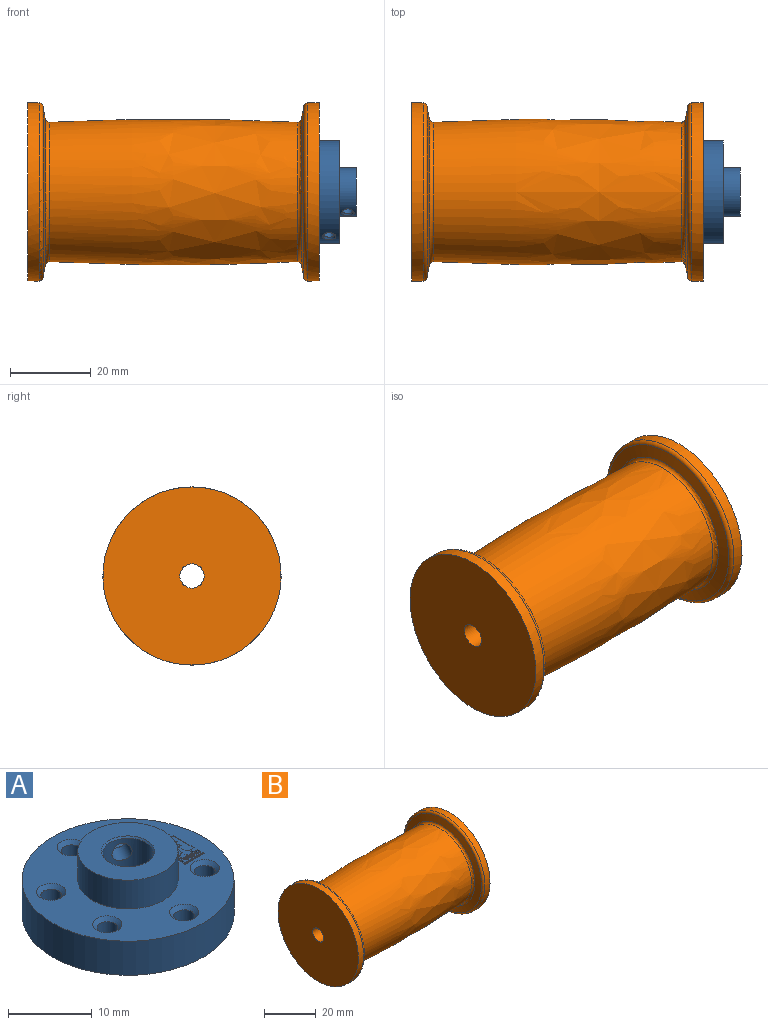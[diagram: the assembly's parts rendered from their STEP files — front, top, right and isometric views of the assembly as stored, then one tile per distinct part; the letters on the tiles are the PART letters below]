
ASSEMBLY  parts=2 mates=1
PART A: 277 faces, bbox 25.4x25.4x9.2 mm
  f0: bspline ~3.27x2.94mm, area 5.6mm2, adj f17,f26
  f1: bspline ~3.07x2.86mm, area 4.8mm2, adj f16,f19
  f2: cone r=3mm half-angle=45deg, axis (0,0,1), area 5.5mm2, adj f18,f29
  f3: cone r=3.2mm half-angle=45deg, axis (0,0,-1), area 5.5mm2, adj f18,f28
  f4: cone r=1.25mm half-angle=45deg, axis (0,0,1), area 6.7mm2, adj f25,f27
  f5: cone r=1.25mm half-angle=45deg, axis (0,0,1), area 6.7mm2, adj f24,f27
  f6: cone r=1.25mm half-angle=45deg, axis (0,0,1), area 6.7mm2, adj f23,f27
  f7: cone r=1.25mm half-angle=45deg, axis (0,0,1), area 6.7mm2, adj f22,f27
  f8: cone r=1.25mm half-angle=45deg, axis (0,0,1), area 6.7mm2, adj f21,f27
  f9: cone r=1.25mm half-angle=45deg, axis (0,0,1), area 6.7mm2, adj f20,f27
  f10: cone r=1.75mm half-angle=45deg, axis (0,0,-1), area 6.7mm2, adj f20,f28
  f11: cone r=1.75mm half-angle=45deg, axis (0,0,-1), area 6.7mm2, adj f25,f28
  f12: cone r=1.75mm half-angle=45deg, axis (0,0,-1), area 6.7mm2, adj f24,f28
  f13: cone r=1.75mm half-angle=45deg, axis (0,0,-1), area 6.7mm2, adj f23,f28
  f14: cone r=1.75mm half-angle=45deg, axis (0,0,-1), area 6.7mm2, adj f22,f28
  f15: cone r=1.75mm half-angle=45deg, axis (0,0,-1), area 6.7mm2, adj f21,f28
  f16: cylinder r=1.25mm len=3.72mm, axis (0.5,0.87,0), area 20.5mm2, adj f1,f18
  f17: cylinder r=1.25mm len=9.5mm, axis (0.5,0.87,0), area 73.3mm2, adj f0,f18
  f18: cylinder r=3mm len=8.8mm, axis (0,0,1), area 155.8mm2, adj f2,f3,f16,f17
  f19: cylinder r=6mm len=12mm, axis (0,0,-1), area 150.3mm2, adj f1,f27,f29
  f20: cylinder r=1.25mm len=4mm, axis (0,0,1), area 31.4mm2, adj f9,f10
  f21: cylinder r=1.25mm len=4mm, axis (0,0,1), area 31.4mm2, adj f8,f15
  f22: cylinder r=1.25mm len=4mm, axis (0,0,1), area 31.4mm2, adj f7,f14
  f23: cylinder r=1.25mm len=4mm, axis (0,0,1), area 31.4mm2, adj f6,f13
  f24: cylinder r=1.25mm len=4mm, axis (0,0,1), area 31.4mm2, adj f5,f12
  f25: cylinder r=1.25mm len=4mm, axis (0,0,1), area 31.4mm2, adj f4,f11
  f26: cylinder r=12.7mm len=25.4mm, axis (0,0,-1), area 390.2mm2, adj f0,f27,f28
  f27: plane 25.4x25.4mm, normal (0,0,1), area 325.6mm2, adj f4,f5,f6,f7,f8,f9,f19,f26
  f28: plane 25.4x25.4mm, normal (0,0,-1), area 416.8mm2, adj f3,f10,f11,f12,f13,f14,f15,f26
  f29: plane 12x12mm, normal (0,0,1), area 80.9mm2, adj f2,f19
  f30: plane 0.05x0.04mm, normal (0,-1,0), area 0mm2, adj f27,f31,f42,f43
  f31: plane 0.22x0.06mm, normal (-0.97,0.25,0), area 0mm2, adj f27,f30,f32,f43
  f32: plane 0.05x0.03mm, normal (0,1,0), area 0mm2, adj f27,f31,f33,f43
  f33: plane 0.17x0.06mm, normal (0.95,0.31,0), area 0mm2, adj f27,f32,f34,f43
  f34: plane 0.17x0.06mm, normal (-0.95,0.31,0), area 0mm2, adj f27,f33,f35,f43
  f35: plane 0.05x0.03mm, normal (0,1,0), area 0mm2, adj f27,f34,f36,f43
  f36: plane 0.22x0.06mm, normal (0.97,0.25,0), area 0mm2, adj f27,f35,f37,f43
  f37: plane 0.05x0.04mm, normal (0,-1,0), area 0mm2, adj f27,f36,f38,f43
  f38: plane 0.17x0.05mm, normal (-0.97,-0.23,0), area 0mm2, adj f27,f37,f39,f43
  f39: plane 0.17x0.06mm, normal (0.95,-0.31,0), area 0mm2, adj f27,f38,f40,f43
  f40: plane 0.05x0.03mm, normal (0,-1,0), area 0mm2, adj f27,f39,f41,f43
  f41: plane 0.17x0.06mm, normal (-0.95,-0.31,0), area 0mm2, adj f27,f40,f42,f43
  f42: plane 0.17x0.05mm, normal (0.98,-0.21,0), area 0mm2, adj f27,f30,f41,f43
  f43: plane 0.3x0.22mm, normal (0,0,1), area 0mm2, adj f30,f31,f32,f33,f34,f35,f36,f37
  f44: plane 0.05x0.04mm, normal (0,-1,0), area 0mm2, adj f27,f45,f56,f57
  f45: plane 0.22x0.06mm, normal (-0.97,0.25,0), area 0mm2, adj f27,f44,f46,f57
  f46: plane 0.05x0.03mm, normal (0,1,0), area 0mm2, adj f27,f45,f47,f57
  f47: plane 0.17x0.06mm, normal (0.95,0.31,0), area 0mm2, adj f27,f46,f48,f57
  f48: plane 0.17x0.06mm, normal (-0.95,0.31,0), area 0mm2, adj f27,f47,f49,f57
  f49: plane 0.05x0.03mm, normal (0,1,0), area 0mm2, adj f27,f48,f50,f57
  f50: plane 0.22x0.06mm, normal (0.97,0.25,0), area 0mm2, adj f27,f49,f51,f57
  f51: plane 0.05x0.04mm, normal (0,-1,0), area 0mm2, adj f27,f50,f52,f57
  f52: plane 0.17x0.05mm, normal (-0.97,-0.23,0), area 0mm2, adj f27,f51,f53,f57
  f53: plane 0.17x0.06mm, normal (0.95,-0.31,0), area 0mm2, adj f27,f52,f54,f57
  f54: plane 0.05x0.03mm, normal (0,-1,0), area 0mm2, adj f27,f53,f55,f57
  f55: plane 0.17x0.06mm, normal (-0.95,-0.31,0), area 0mm2, adj f27,f54,f56,f57
  f56: plane 0.17x0.05mm, normal (0.98,-0.21,0), area 0mm2, adj f27,f44,f55,f57
  f57: plane 0.3x0.22mm, normal (0,0,1), area 0mm2, adj f44,f45,f46,f47,f48,f49,f50,f51
  f58: plane 0.05x0.04mm, normal (0,-1,0), area 0mm2, adj f27,f59,f70,f71
  f59: plane 0.22x0.06mm, normal (-0.97,0.25,0), area 0mm2, adj f27,f58,f60,f71
  f60: plane 0.05x0.03mm, normal (0,1,0), area 0mm2, adj f27,f59,f61,f71
  f61: plane 0.17x0.06mm, normal (0.95,0.31,0), area 0mm2, adj f27,f60,f62,f71
  f62: plane 0.17x0.06mm, normal (-0.95,0.31,0), area 0mm2, adj f27,f61,f63,f71
  f63: plane 0.05x0.03mm, normal (0,1,0), area 0mm2, adj f27,f62,f64,f71
  f64: plane 0.22x0.06mm, normal (0.97,0.25,0), area 0mm2, adj f27,f63,f65,f71
  f65: plane 0.05x0.04mm, normal (0,-1,0), area 0mm2, adj f27,f64,f66,f71
  f66: plane 0.17x0.05mm, normal (-0.97,-0.23,0), area 0mm2, adj f27,f65,f67,f71
  f67: plane 0.17x0.06mm, normal (0.95,-0.31,0), area 0mm2, adj f27,f66,f68,f71
  f68: plane 0.05x0.03mm, normal (0,-1,0), area 0mm2, adj f27,f67,f69,f71
  f69: plane 0.17x0.06mm, normal (-0.95,-0.31,0), area 0mm2, adj f27,f68,f70,f71
  f70: plane 0.17x0.05mm, normal (0.98,-0.21,0), area 0mm2, adj f27,f58,f69,f71
  f71: plane 0.3x0.22mm, normal (0,0,1), area 0mm2, adj f58,f59,f60,f61,f62,f63,f64,f65
  f72: plane 0.06x0.05mm, normal (-1,0,0), area 0mm2, adj f27,f73,f75,f76
  f73: plane 0.05x0.05mm, normal (0,1,0), area 0mm2, adj f27,f72,f74,f76
  f74: plane 0.06x0.05mm, normal (1,0,0), area 0mm2, adj f27,f73,f75,f76
  f75: plane 0.05x0.05mm, normal (0,-1,0), area 0mm2, adj f27,f72,f74,f76
  f76: plane 0.06x0.05mm, normal (0,0,1), area 0mm2, adj f72,f73,f74,f75
  f77: extruded ~0.11x0.08mm, area 0mm2, adj f27,f78,f86,f87
  f78: extruded ~0.09x0.05mm, area 0mm2, adj f27,f77,f79,f87
  f79: cylinder r=0.09mm len=0.07mm, axis (0,0,-1), area 0mm2, adj f27,f78,f80,f87
  f80: cylinder r=0.11mm len=0.06mm, axis (0,0,-1), area 0mm2, adj f27,f79,f81,f87
  f81: plane 0.09x0.05mm, normal (-1,0,0), area 0mm2, adj f27,f80,f82,f87
  f82: plane 0.05x0.04mm, normal (0,1,0), area 0mm2, adj f27,f81,f83,f87
  f83: plane 0.3x0.05mm, normal (1,0,0), area 0mm2, adj f27,f82,f84,f87
  f84: plane 0.05x0.04mm, normal (0,-1,0), area 0mm2, adj f27,f83,f85,f87
  f85: plane 0.05x0.02mm, normal (-1,0,0), area 0mm2, adj f27,f84,f86,f87
  f86: extruded ~0.07x0.05mm, area 0mm2, adj f27,f77,f85,f87
  f87: plane 0.31x0.19mm, normal (0,0,1), area 0mm2, adj f77,f78,f79,f80,f81,f82,f83,f84
  f88: extruded ~0.08x0.06mm, area 0mm2, adj f87,f89,f92,f93
  f89: cylinder r=0.14mm len=0.05mm, axis (0,0,1), area 0mm2, adj f87,f88,f90,f93
  f90: plane 0.13x0.05mm, normal (-1,0,0), area 0mm2, adj f87,f89,f91,f93
  f91: extruded ~0.06x0.05mm, area 0mm2, adj f87,f90,f92,f93
  f92: extruded ~0.08x0.05mm, area 0mm2, adj f87,f88,f91,f93
  f93: plane 0.17x0.12mm, normal (0,0,1), area 0mm2, adj f88,f89,f90,f91,f92
  f94: extruded ~0.12x0.1mm, area 0mm2, adj f27,f95,f97,f98
  f95: extruded ~0.12x0.1mm, area 0mm2, adj f27,f94,f96,f98
  f96: extruded ~0.12x0.1mm, area 0mm2, adj f27,f95,f97,f98
  f97: extruded ~0.12x0.1mm, area 0mm2, adj f27,f94,f96,f98
  f98: plane 0.24x0.2mm, normal (0,0,1), area 0mm2, adj f94,f95,f96,f97,f99,f100,f101,f102
  f99: extruded ~0.08x0.06mm, area 0mm2, adj f98,f100,f102,f103
  f100: extruded ~0.08x0.06mm, area 0mm2, adj f98,f99,f101,f103
  f101: extruded ~0.08x0.06mm, area 0mm2, adj f98,f100,f102,f103
  f102: extruded ~0.08x0.06mm, area 0mm2, adj f98,f99,f101,f103
  f103: plane 0.17x0.13mm, normal (0,0,1), area 0mm2, adj f99,f100,f101,f102
  f104: plane 0.31x0.05mm, normal (-1,0,0), area 0mm2, adj f27,f105,f107,f108
  f105: plane 0.05x0.04mm, normal (0,1,0), area 0mm2, adj f27,f104,f106,f108
  f106: plane 0.31x0.05mm, normal (1,0,0), area 0mm2, adj f27,f105,f107,f108
  f107: plane 0.05x0.04mm, normal (0,-1,0), area 0mm2, adj f27,f104,f106,f108
  f108: plane 0.31x0.04mm, normal (0,0,1), area 0mm2, adj f104,f105,f106,f107
  f109: extruded ~0.12x0.1mm, area 0mm2, adj f27,f110,f112,f113
  f110: extruded ~0.12x0.1mm, area 0mm2, adj f27,f109,f111,f113
  f111: extruded ~0.12x0.1mm, area 0mm2, adj f27,f110,f112,f113
  f112: extruded ~0.12x0.1mm, area 0mm2, adj f27,f109,f111,f113
  f113: plane 0.24x0.2mm, normal (0,0,1), area 0mm2, adj f109,f110,f111,f112,f114,f115,f116,f117
  f114: extruded ~0.08x0.06mm, area 0mm2, adj f113,f115,f117,f118
  f115: extruded ~0.08x0.06mm, area 0mm2, adj f113,f114,f116,f118
  f116: extruded ~0.08x0.06mm, area 0mm2, adj f113,f115,f117,f118
  f117: extruded ~0.08x0.06mm, area 0mm2, adj f113,f114,f116,f118
  f118: plane 0.17x0.13mm, normal (0,0,1), area 0mm2, adj f114,f115,f116,f117
  f119: plane 0.31x0.05mm, normal (-1,0,0), area 0mm2, adj f27,f120,f122,f123
  f120: plane 0.05x0.04mm, normal (0,1,0), area 0mm2, adj f27,f119,f121,f123
  f121: plane 0.31x0.05mm, normal (1,0,0), area 0mm2, adj f27,f120,f122,f123
  f122: plane 0.05x0.04mm, normal (0,-1,0), area 0mm2, adj f27,f119,f121,f123
  f123: plane 0.31x0.04mm, normal (0,0,1), area 0mm2, adj f119,f120,f121,f122
  f124: plane 0.22x0.05mm, normal (-1,0,0), area 0mm2, adj f27,f125,f136,f137
  f125: plane 0.05x0.04mm, normal (0,1,0), area 0mm2, adj f27,f124,f126,f137
  f126: plane 0.05x0.02mm, normal (1,0,0), area 0mm2, adj f27,f125,f127,f137
  f127: extruded ~0.07x0.05mm, area 0mm2, adj f27,f126,f128,f137
  f128: extruded ~0.08x0.07mm, area 0mm2, adj f27,f127,f129,f137
  f129: plane 0.14x0.05mm, normal (1,0,0), area 0mm2, adj f27,f128,f130,f137
  f130: plane 0.05x0.04mm, normal (0,-1,0), area 0mm2, adj f27,f129,f131,f137
  f131: plane 0.13x0.05mm, normal (-1,0,0), area 0mm2, adj f27,f130,f132,f137
  f132: extruded ~0.05x0.05mm, area 0mm2, adj f27,f131,f133,f137
  f133: extruded ~0.05x0.04mm, area 0mm2, adj f27,f132,f134,f137
  f134: extruded ~0.06x0.05mm, area 0mm2, adj f27,f133,f135,f137
  f135: plane 0.17x0.05mm, normal (1,0,0), area 0mm2, adj f27,f134,f136,f137
  f136: plane 0.05x0.04mm, normal (0,-1,0), area 0mm2, adj f27,f124,f135,f137
  f137: plane 0.23x0.18mm, normal (0,0,1), area 0mm2, adj f124,f125,f126,f127,f128,f129,f130,f131
  f138: plane 0.06x0.05mm, normal (-1,0,0), area 0mm2, adj f27,f139,f141,f142
  f139: plane 0.05x0.05mm, normal (0,1,0), area 0mm2, adj f27,f138,f140,f142
  f140: plane 0.06x0.05mm, normal (1,0,0), area 0mm2, adj f27,f139,f141,f142
  f141: plane 0.05x0.05mm, normal (0,-1,0), area 0mm2, adj f27,f138,f140,f142
  f142: plane 0.06x0.05mm, normal (0,0,1), area 0mm2, adj f138,f139,f140,f141
  f143: plane 0.05x0.04mm, normal (-1,0,0), area 0mm2, adj f27,f144,f156,f157
  f144: extruded ~0.07x0.05mm, area 0mm2, adj f27,f143,f145,f157
  f145: extruded ~0.08x0.05mm, area 0mm2, adj f27,f144,f146,f157
  f146: extruded ~0.09x0.05mm, area 0mm2, adj f27,f145,f147,f157
  f147: extruded ~0.12x0.11mm, area 0mm2, adj f27,f146,f148,f157
  f148: extruded ~0.07x0.05mm, area 0mm2, adj f27,f147,f149,f157
  f149: plane 0.05x0.04mm, normal (-1,0,0), area 0mm2, adj f27,f148,f150,f157
  f150: plane 0.05x0mm, normal (0,1,0), area 0mm2, adj f27,f149,f151,f157
  f151: extruded ~0.07x0.05mm, area 0mm2, adj f27,f150,f152,f157
  f152: extruded ~0.08x0.07mm, area 0mm2, adj f27,f151,f153,f157
  f153: extruded ~0.08x0.07mm, area 0mm2, adj f27,f152,f154,f157
  f154: cylinder r=0.09mm len=0.05mm, axis (0,0,1), area 0mm2, adj f27,f153,f155,f157
  f155: cylinder r=0.16mm len=0.05mm, axis (0,0,1), area 0mm2, adj f27,f154,f156,f157
  f156: plane 0.05x0mm, normal (0,-1,0), area 0mm2, adj f27,f143,f155,f157
  f157: plane 0.23x0.18mm, normal (0,0,1), area 0mm2, adj f143,f144,f145,f146,f147,f148,f149,f150
  f158: extruded ~0.12x0.1mm, area 0mm2, adj f27,f159,f161,f162
  f159: extruded ~0.12x0.1mm, area 0mm2, adj f27,f158,f160,f162
  f160: extruded ~0.12x0.1mm, area 0mm2, adj f27,f159,f161,f162
  f161: extruded ~0.12x0.1mm, area 0mm2, adj f27,f158,f160,f162
  f162: plane 0.24x0.2mm, normal (0,0,1), area 0mm2, adj f158,f159,f160,f161,f163,f164,f165,f166
  f163: extruded ~0.08x0.06mm, area 0mm2, adj f162,f164,f166,f167
  f164: extruded ~0.08x0.06mm, area 0mm2, adj f162,f163,f165,f167
  f165: extruded ~0.08x0.06mm, area 0mm2, adj f162,f164,f166,f167
  f166: extruded ~0.08x0.06mm, area 0mm2, adj f162,f163,f165,f167
  f167: plane 0.17x0.13mm, normal (0,0,1), area 0mm2, adj f163,f164,f165,f166
  f168: plane 0.14x0.05mm, normal (-1,0,0), area 0mm2, adj f27,f169,f189,f190
  f169: plane 0.05x0.04mm, normal (0,1,0), area 0mm2, adj f27,f168,f170,f190
  f170: plane 0.13x0.05mm, normal (1,0,0), area 0mm2, adj f27,f169,f171,f190
  f171: extruded ~0.05x0.05mm, area 0mm2, adj f27,f170,f172,f190
  f172: extruded ~0.05x0.04mm, area 0mm2, adj f27,f171,f173,f190
  f173: extruded ~0.06x0.05mm, area 0mm2, adj f27,f172,f174,f190
  f174: cylinder r=0.19mm len=0.05mm, axis (0,0,-1), area 0mm2, adj f27,f173,f175,f190
  f175: plane 0.14x0.05mm, normal (-1,0,0), area 0mm2, adj f27,f174,f176,f190
  f176: plane 0.05x0.04mm, normal (0,1,0), area 0mm2, adj f27,f175,f177,f190
  f177: plane 0.13x0.05mm, normal (1,0,0), area 0mm2, adj f27,f176,f178,f190
  f178: extruded ~0.05x0.05mm, area 0mm2, adj f27,f177,f179,f190
  f179: extruded ~0.05x0.04mm, area 0mm2, adj f27,f178,f180,f190
  f180: extruded ~0.06x0.05mm, area 0mm2, adj f27,f179,f181,f190
  f181: plane 0.17x0.05mm, normal (-1,0,0), area 0mm2, adj f27,f180,f182,f190
  f182: plane 0.05x0.04mm, normal (0,1,0), area 0mm2, adj f27,f181,f183,f190
  f183: plane 0.22x0.05mm, normal (1,0,0), area 0mm2, adj f27,f182,f184,f190
  f184: plane 0.05x0.04mm, normal (0,-1,0), area 0mm2, adj f27,f183,f185,f190
  f185: plane 0.05x0.02mm, normal (-1,0,0), area 0mm2, adj f27,f184,f186,f190
  f186: extruded ~0.07x0.05mm, area 0mm2, adj f27,f185,f187,f190
  f187: cylinder r=0.06mm len=0.06mm, axis (0,0,-1), area 0mm2, adj f27,f186,f188,f190
  f188: extruded ~0.08x0.05mm, area 0mm2, adj f27,f187,f189,f190
  f189: extruded ~0.08x0.07mm, area 0mm2, adj f27,f168,f188,f190
  f190: plane 0.32x0.23mm, normal (0,0,1), area 0mm2, adj f168,f169,f170,f171,f172,f173,f174,f175
  f191: extruded ~0.27x0.26mm, area 0mm2, adj f27,f192,f200,f201
  f192: plane 0.32x0.05mm, normal (1,0,0), area 0mm2, adj f27,f191,f193,f201
  f193: plane 0.18x0.05mm, normal (0,-1,0), area 0mm2, adj f27,f192,f194,f201
  f194: plane 0.33x0.05mm, normal (-1,0,0), area 0mm2, adj f27,f193,f195,f201
  f195: extruded ~0.1x0.08mm, area 0mm2, adj f27,f194,f196,f201
  f196: extruded ~0.09x0.08mm, area 0mm2, adj f27,f195,f197,f201
  f197: plane 0.33x0.05mm, normal (1,0,0), area 0mm2, adj f27,f196,f198,f201
  f198: plane 0.18x0.05mm, normal (0,-1,0), area 0mm2, adj f27,f197,f199,f201
  f199: plane 0.32x0.05mm, normal (-1,0,0), area 0mm2, adj f27,f198,f200,f201
  f200: extruded ~0.27x0.27mm, area 0mm2, adj f27,f191,f199,f201
  f201: plane 0.59x0.54mm, normal (0,0,1), area 0.2mm2, adj f191,f192,f193,f194,f195,f196,f197,f198
  f202: extruded ~0.3x0.29mm, area 0mm2, adj f27,f203,f207,f208
  f203: plane 0.05x0mm, normal (1,0,0), area 0mm2, adj f27,f202,f204,f208
  f204: extruded ~0.31x0.29mm, area 0mm2, adj f27,f203,f205,f208
  f205: extruded ~0.3x0.29mm, area 0mm2, adj f27,f204,f206,f208
  f206: plane 0.05x0mm, normal (-1,0,0), area 0mm2, adj f27,f205,f207,f208
  f207: extruded ~0.31x0.29mm, area 0mm2, adj f27,f202,f206,f208
  f208: plane 0.61x0.59mm, normal (0,0,1), area 0.2mm2, adj f202,f203,f204,f205,f206,f207,f209,f210
  f209: extruded ~0.14x0.13mm, area 0mm2, adj f208,f210,f214,f215
  f210: extruded ~0.14x0.13mm, area 0mm2, adj f208,f209,f211,f215
  f211: plane 0.05x0mm, normal (-1,0,0), area 0mm2, adj f208,f210,f212,f215
  f212: extruded ~0.14x0.13mm, area 0mm2, adj f208,f211,f213,f215
  f213: extruded ~0.14x0.13mm, area 0mm2, adj f208,f212,f214,f215
  f214: plane 0.05x0mm, normal (1,0,0), area 0mm2, adj f208,f209,f213,f215
  f215: plane 0.28x0.26mm, normal (0,0,1), area 0.1mm2, adj f209,f210,f211,f212,f213,f214
  f216: plane 0.89x0.05mm, normal (1,0,0), area 0mm2, adj f27,f217,f219,f220
  f217: plane 0.19x0.05mm, normal (0,-1,0), area 0mm2, adj f27,f216,f218,f220
  f218: plane 0.89x0.05mm, normal (-1,0,0), area 0mm2, adj f27,f217,f219,f220
  f219: plane 0.19x0.05mm, normal (0,1,0), area 0mm2, adj f27,f216,f218,f220
  f220: plane 0.89x0.19mm, normal (0,0,1), area 0.2mm2, adj f216,f217,f218,f219
  f221: extruded ~0.3x0.29mm, area 0mm2, adj f27,f222,f226,f227
  f222: plane 0.05x0mm, normal (1,0,0), area 0mm2, adj f27,f221,f223,f227
  f223: extruded ~0.31x0.29mm, area 0mm2, adj f27,f222,f224,f227
  f224: extruded ~0.3x0.29mm, area 0mm2, adj f27,f223,f225,f227
  f225: plane 0.05x0mm, normal (-1,0,0), area 0mm2, adj f27,f224,f226,f227
  f226: extruded ~0.31x0.29mm, area 0mm2, adj f27,f221,f225,f227
  f227: plane 0.61x0.59mm, normal (0,0,1), area 0.2mm2, adj f221,f222,f223,f224,f225,f226,f228,f229
  f228: extruded ~0.14x0.13mm, area 0mm2, adj f227,f229,f233,f234
  f229: extruded ~0.14x0.13mm, area 0mm2, adj f227,f228,f230,f234
  f230: plane 0.05x0mm, normal (-1,0,0), area 0mm2, adj f227,f229,f231,f234
  f231: extruded ~0.14x0.13mm, area 0mm2, adj f227,f230,f232,f234
  f232: extruded ~0.14x0.13mm, area 0mm2, adj f227,f231,f233,f234
  f233: plane 0.05x0mm, normal (1,0,0), area 0mm2, adj f227,f228,f232,f234
  f234: plane 0.28x0.26mm, normal (0,0,1), area 0.1mm2, adj f228,f229,f230,f231,f232,f233
  f235: plane 0.89x0.05mm, normal (1,0,0), area 0mm2, adj f27,f236,f238,f239
  f236: plane 0.19x0.05mm, normal (0,-1,0), area 0mm2, adj f27,f235,f237,f239
  f237: plane 0.89x0.05mm, normal (-1,0,0), area 0mm2, adj f27,f236,f238,f239
  f238: plane 0.19x0.05mm, normal (0,1,0), area 0mm2, adj f27,f235,f237,f239
  f239: plane 0.89x0.19mm, normal (0,0,1), area 0.2mm2, adj f235,f236,f237,f238
  f240: extruded ~0.33x0.3mm, area 0mm2, adj f27,f241,f247,f248
  f241: plane 0.05x0mm, normal (-1,0,0), area 0mm2, adj f27,f240,f242,f248
  f242: extruded ~0.35x0.3mm, area 0mm2, adj f27,f241,f243,f248
  f243: plane 0.09x0.05mm, normal (0,1,0), area 0mm2, adj f27,f242,f244,f248
  f244: plane 0.3x0.05mm, normal (-1,0,0), area 0mm2, adj f27,f243,f245,f248
  f245: plane 0.19x0.05mm, normal (0,1,0), area 0mm2, adj f27,f244,f246,f248
  f246: plane 0.89x0.05mm, normal (1,0,0), area 0mm2, adj f27,f245,f247,f248
  f247: plane 0.29x0.05mm, normal (0,-1,0), area 0mm2, adj f27,f240,f246,f248
  f248: plane 0.89x0.62mm, normal (0,0,1), area 0.3mm2, adj f240,f241,f242,f243,f244,f245,f246,f247
  f249: extruded ~0.15x0.13mm, area 0mm2, adj f248,f250,f254,f255
  f250: plane 0.09x0.05mm, normal (0,-1,0), area 0mm2, adj f248,f249,f251,f255
  f251: plane 0.26x0.05mm, normal (-1,0,0), area 0mm2, adj f248,f250,f252,f255
  f252: plane 0.09x0.05mm, normal (0,1,0), area 0mm2, adj f248,f251,f253,f255
  f253: extruded ~0.15x0.13mm, area 0mm2, adj f248,f252,f254,f255
  f254: plane 0.05x0mm, normal (1,0,0), area 0mm2, adj f248,f249,f253,f255
  f255: plane 0.26x0.24mm, normal (0,0,1), area 0.1mm2, adj f249,f250,f251,f252,f253,f254
  f256: extruded ~0.58x0.32mm, area 0mm2, adj f27,f257,f275,f276
  f257: extruded ~1.29x0.14mm, area 0.1mm2, adj f27,f256,f258,f276
  f258: sphere r=1.78mm, area 0mm2, adj f27,f257,f259,f276
  f259: extruded ~0.61x0.32mm, area 0mm2, adj f27,f258,f260,f276
  f260: extruded ~0.54x0.35mm, area 0mm2, adj f27,f259,f261,f276
  f261: extruded ~0.8x0.16mm, area 0mm2, adj f27,f260,f262,f276
  f262: extruded ~0.59x0.59mm, area 0mm2, adj f27,f261,f263,f276
  f263: extruded ~0.69x0.09mm, area 0mm2, adj f27,f262,f264,f276
  f264: extruded ~0.73x0.32mm, area 0mm2, adj f27,f263,f265,f276
  f265: extruded ~0.62x0.2mm, area 0mm2, adj f27,f264,f266,f276
  f266: extruded ~0.66x0.16mm, area 0mm2, adj f27,f265,f267,f276
  f267: extruded ~0.62x0.37mm, area 0mm2, adj f27,f266,f268,f276
  f268: extruded ~1.29x0.16mm, area 0.1mm2, adj f27,f267,f269,f276
  f269: extruded ~0.38x0.09mm, area 0mm2, adj f27,f268,f270,f276
  f270: extruded ~0.36x0.21mm, area 0mm2, adj f27,f269,f271,f276
  f271: plane 0.71x0.05mm, normal (0,1,0), area 0mm2, adj f27,f270,f272,f276
  f272: plane 3.49x0.05mm, normal (1,0,0), area 0.2mm2, adj f27,f271,f273,f276
  f273: plane 3.17x0.05mm, normal (0,-1,0), area 0.2mm2, adj f27,f272,f274,f276
  f274: plane 3.49x0.05mm, normal (-1,0,0), area 0.2mm2, adj f27,f273,f275,f276
  f275: plane 0.62x0.05mm, normal (0,1,0), area 0mm2, adj f27,f256,f274,f276
  f276: plane 3.49x3.17mm, normal (0,0,1), area 8.5mm2, adj f256,f257,f258,f259,f260,f261,f262,f263
PART B: 24 faces, bbox 72x47.6x47.6 mm
  f0: cone r=0mm half-angle=59deg, axis (1,0,0), area 5.7mm2, adj f1
  f1: cylinder r=1.25mm len=8mm, axis (1,0,0), area 62.8mm2, adj f0,f13
  f2: cone r=0mm half-angle=59deg, axis (1,0,0), area 5.7mm2, adj f3
  f3: cylinder r=1.25mm len=8mm, axis (1,0,0), area 62.8mm2, adj f2,f13
  f4: cone r=0mm half-angle=59deg, axis (1,0,0), area 5.7mm2, adj f5
  f5: cylinder r=1.25mm len=8mm, axis (1,0,0), area 62.8mm2, adj f4,f13
  f6: cone r=0mm half-angle=59deg, axis (1,0,0), area 5.7mm2, adj f7
  f7: cylinder r=1.25mm len=8mm, axis (1,0,0), area 62.8mm2, adj f6,f13
  f8: cone r=0mm half-angle=59deg, axis (1,0,0), area 5.7mm2, adj f9
  f9: cylinder r=1.25mm len=8mm, axis (1,0,0), area 62.8mm2, adj f8,f13
  f10: cone r=22mm half-angle=80deg, axis (-1,0,0), area 391.6mm2, adj f18,f19
  f11: cylinder r=22mm len=44mm, axis (-1,0,0), area 388.4mm2, adj f12,f19
  f12: plane 44x44mm, normal (-1,0,0), area 1492.3mm2, adj f11,f21
  f13: plane 44x44mm, normal (1,0,0), area 1462.8mm2, adj f1,f3,f5,f7,f9,f14,f21,f23
  f14: cylinder r=22mm len=44mm, axis (-1,0,0), area 388.4mm2, adj f13,f20
  f15: cone r=22mm half-angle=80deg, axis (1,0,0), area 391.6mm2, adj f17,f20
  f16: revolved ~61.24x36mm, area 6828.3mm2, adj f17,f18
  f17: torus R=18.22mm, axis (-1,0,0), area 159.2mm2, adj f15,f16
  f18: torus R=18.22mm, axis (-1,0,0), area 159.2mm2, adj f10,f16
  f19: torus R=21mm, axis (1,0,0), area 190.4mm2, adj f10,f11
  f20: torus R=21mm, axis (1,0,0), area 190.4mm2, adj f14,f15
  f21: cylinder r=3mm len=72mm, axis (1,0,0), area 1357.2mm2, adj f12,f13
  f22: cone r=0mm half-angle=59deg, axis (1,0,0), area 5.7mm2, adj f23
  f23: cylinder r=1.25mm len=8mm, axis (1,0,0), area 62.8mm2, adj f13,f22
PLACE A rot(axis=(-0.58,0.58,-0.58),120deg) t=(39.19,17.81,26.11)mm
PLACE B t=(0.69,17.81,26.11)mm
MATE cylindrical A.f2 <-> B.f10  axis (-1,0,0) through (36.69,17.81,26.11)mm
